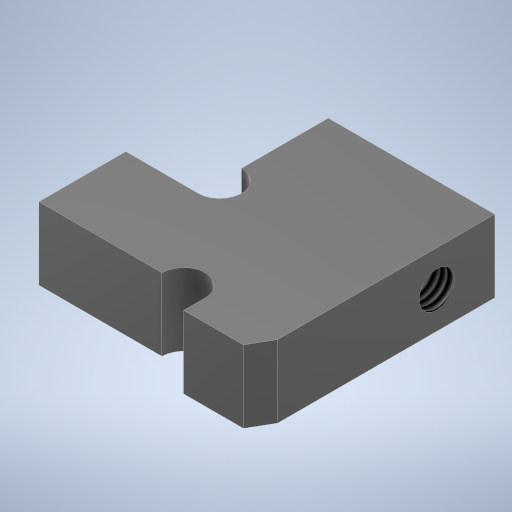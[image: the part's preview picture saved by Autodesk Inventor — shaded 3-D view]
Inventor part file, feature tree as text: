
AUTODESK INVENTOR PART (.ipt)
format: ipt  version: 2024.2 (Build 282272000, 272)  size: 235,008 bytes
history: native  units: mm
features: sketch x2, extrude x1, hole x1
ambient origin geometry x8: Origin, YZ Plane, XZ Plane, XY Plane, X Axis, Y Axis, Z Axis, Center Point
bodies: Solid1 (feature_tree)
feature tree (4):
  extrude  "Extrusion1"  Depth=6.0mm
  hole  "Hole1"  [1 undecoded]
  sketch  "Sketch1"  dims[d0=5.0mm d1=6.0mm]
  sketch  "Sketch2"  dims[d2=15.0mm d3=4.5mm d4=1.5mm d5=1.5mm d6=6.5mm d7=30.0deg d8=5.0mm d9=5.0mm d10=0.0mm d11=2.459mm d12=6.0mm d13=6.5mm d14=3.5mm d15=90.0deg d16=8.0mm d17=20.594885mm d18=4.0mm]
note: 1 required parameter value undecoded (feature->parameter linkage not recoverable at this tier; creation-order binding heuristic only, values carry confidence <= 0.55)
